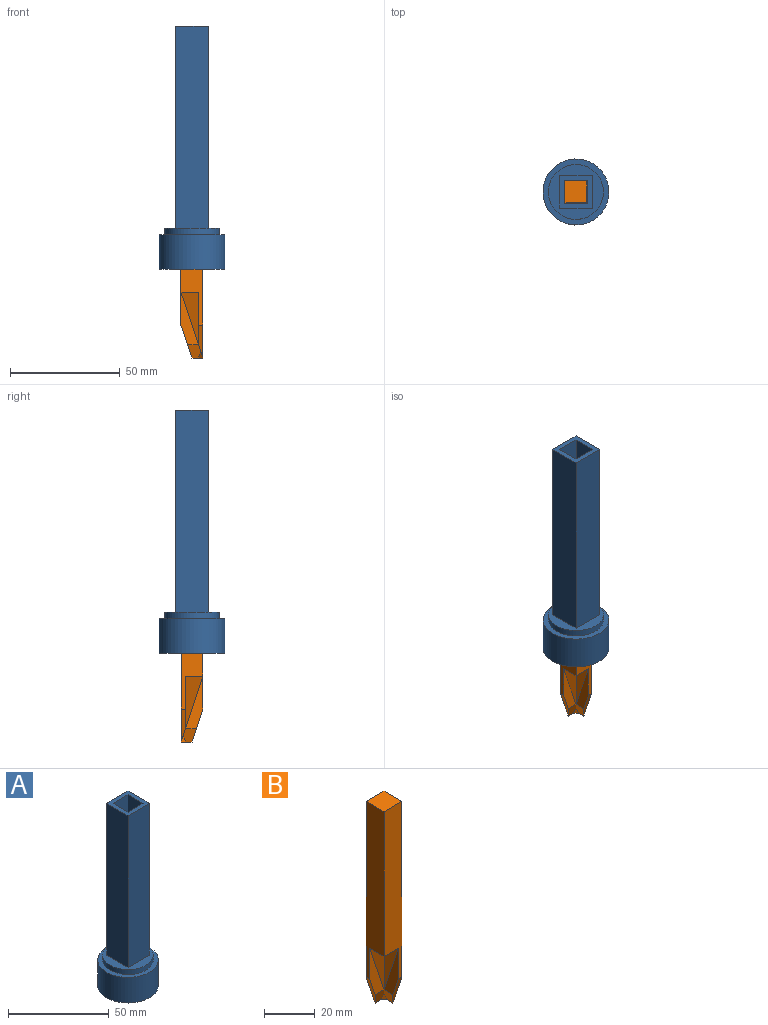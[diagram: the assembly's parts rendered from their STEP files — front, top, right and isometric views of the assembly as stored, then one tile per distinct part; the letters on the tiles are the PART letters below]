
ASSEMBLY  parts=2 mates=1
PART A: 21 faces, bbox 30x30x110.5 mm
  f0: plane 92x15mm, normal (0,-1,0), area 1380mm2, adj f1,f3,f9,f20
  f1: plane 92x15mm, normal (1,0,0), area 1380mm2, adj f0,f2,f9,f20
  f2: plane 92x15mm, normal (0,1,0), area 1380mm2, adj f1,f3,f9,f20
  f3: plane 92x15mm, normal (-1,0,0), area 1380mm2, adj f0,f2,f9,f20
  f4: plane 20.21x17.5mm, normal (0,0,-1), area 155mm2, adj f5,f6,f7,f8,f11,f12,f13,f14
  f5: plane 95x10.5mm, normal (-1,0,0), area 997.5mm2, adj f4,f6,f8,f9
  f6: plane 95x10.5mm, normal (0,1,0), area 997.5mm2, adj f4,f5,f7,f9
  f7: plane 95x10.5mm, normal (1,0,0), area 997.5mm2, adj f4,f6,f8,f9
  f8: plane 95x10.5mm, normal (0,-1,0), area 997.5mm2, adj f4,f5,f7,f9
  f9: plane 15x15mm, normal (0,0,1), area 114.7mm2, adj f0,f1,f2,f3,f5,f6,f7,f8
  f10: plane 30x30mm, normal (0,0,1), area 216mm2, adj f17,f19
  f11: plane 15.5x10.1mm, normal (1,0,0), area 156.6mm2, adj f4,f12,f16,f18
  f12: plane 15.5x8.75mm, normal (0.5,0.87,0), area 156.6mm2, adj f4,f11,f13,f18
  f13: plane 15.5x8.75mm, normal (-0.5,0.87,0), area 156.6mm2, adj f4,f12,f14,f18
  f14: plane 15.5x10.1mm, normal (-1,0,0), area 156.6mm2, adj f4,f13,f15,f18
  f15: plane 15.5x8.75mm, normal (-0.5,-0.87,0), area 156.6mm2, adj f4,f14,f16,f18
  f16: plane 15.5x8.75mm, normal (0.5,-0.87,0), area 156.6mm2, adj f4,f11,f15,f18
  f17: cylinder r=15mm len=30mm, axis (0,0,1), area 1460.8mm2, adj f10,f18
  f18: plane 30x30mm, normal (0,0,-1), area 441.6mm2, adj f11,f12,f13,f14,f15,f16,f17
  f19: cylinder r=12.5mm len=25mm, axis (0,0,-1), area 235.6mm2, adj f10,f20
  f20: plane 25x25mm, normal (0,0,1), area 265.9mm2, adj f0,f1,f2,f3,f19
PART B: 15 faces, bbox 10x10x100 mm
  f0: plane 85x10mm, normal (0,-1,0), area 730mm2, adj f2,f6,f8,f10,f11,f13
  f1: plane 24x8mm, normal (0,-1,0), area 82.5mm2, adj f2,f3,f4,f12
  f2: plane 85x10mm, normal (-1,0,0), area 730mm2, adj f0,f1,f4,f7,f8,f12
  f3: plane 6x6mm, normal (0,-0.95,-0.32), area 28.5mm2, adj f1,f7,f9,f12,f14
  f4: plane 24x8mm, normal (-0.95,0,-0.32), area 101.2mm2, adj f1,f2,f10
  f5: plane 2x2mm, normal (0,0,-1), area 2mm2, adj f6,f7,f14
  f6: plane 100x10mm, normal (1,0,0), area 962.5mm2, adj f0,f5,f7,f8,f9,f13
  f7: plane 100x10mm, normal (0,1,0), area 962.5mm2, adj f2,f3,f5,f6,f8,f12
  f8: plane 10x10mm, normal (0,0,1), area 100mm2, adj f0,f2,f6,f7
  f9: plane 6x6mm, normal (-0.95,0,-0.32), area 28.5mm2, adj f3,f6,f11,f13,f14
  f10: plane 24x8mm, normal (0,-0.95,-0.32), area 101.2mm2, adj f0,f4,f11
  f11: plane 24x8mm, normal (-1,0,0), area 82.5mm2, adj f0,f9,f10,f13
  f12: plane 15x5mm, normal (-0.95,0,-0.32), area 25.3mm2, adj f1,f2,f3,f7
  f13: plane 15x5mm, normal (0,-0.95,-0.32), area 25.3mm2, adj f0,f6,f9,f11
  f14: plane 3x2mm, normal (-0.71,-0.71,0), area 4.2mm2, adj f3,f5,f9
PLACE A t=(4.71,3.23,0)mm fixed
PLACE B t=(4.71,3.23,-55.95)mm
MATE slider B.f8 <-> A.f17  axis (0,0,1) through (4.71,3.23,44.05)mm
